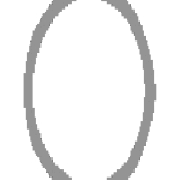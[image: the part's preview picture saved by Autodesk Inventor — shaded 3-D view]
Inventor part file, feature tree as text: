
AUTODESK INVENTOR PART (.ipt)
format: ipt  version: 2021 (Build 250183000, 183)  size: 111,616 bytes
history: native  units: in
note: dims shown in document units (in); Inventor stores cm internally (conversion verified against a paired STEP export)
features: other x4, sketch x3, plane x1
ambient origin geometry x8: Origin, YZ Plane, XZ Plane, XY Plane, X Axis, Y Axis, Z Axis, Center Point
bodies: Solid1 (feature_tree), Body (feature_tree)
feature tree (8):
  other  "Driven Length"
  other  "Frame Generator"
  other  "Start Plane"
  other  "End Plane"
  sketch  "Sketch"  dims[d2=19.6468in d4=-0.0in d5=19.6468in d6=0.12in d7=0.0in d8=90.0deg d9=19.6468in]
  sketch  "Sketch2"  dims[d0=1.0in]
  plane  "Work Plane3"
  sketch  "Sketch3"  dims[d1=0.065in]
